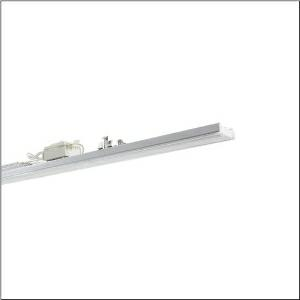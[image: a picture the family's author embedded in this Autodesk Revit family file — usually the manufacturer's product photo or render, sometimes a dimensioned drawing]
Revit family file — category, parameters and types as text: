
# Revit family: licross_21_recessed_mo_52tl11dn455g
name_source: partatom
category: Lighting Fixtures
units: mm (PartAtom-declared; Revit-internal decimal feet)

## family parameters
Cut with Voids When Loaded = No
Host = Face
Light Source = No
Part Type = Normal
Room Calculation Point = No
Round Connector Dimension = Use Diameter
Shared = No

## types (1)
- --- (1 x LED, 5800 lm, 31.8 W, 4000K)
    Apparent Load = 32 VA
    CIE Flux Codes = 89 96 99 100 100
    Color Rendering = 80
    Color Temperature = 4000K
    Default Elevation = 1800 mm
    Description = Licross 21 Recessed MO, luminaire insert, of sheet steel, galvanised, coil coated, white, length: 1.500mm, width: 66mm, height: 67mm, LED rated luminous flux: 5.800lm, light colour: 840, SDCM (Standard Deviation of Colour Matching)MacAdam ≤ 3 SDCM (initial), control gear: DALI 2, with plug, 5-pole, with phase selection, mains connection: 220..240V, AC, 50/60Hz, rated input power: 32W, internal wiring halogen-free, primary light control with lens, of plastic, primary optical cover: cover, of PMMA, light emission: direct distribution, primary light characteristic: symmetric, protection rating (complete): IP40, insulation class (complete): insulation class I (protective earthing), certification: CE, ENEC, VDE, UKCA, protection symbol: D if used in an environment without relevant dust loads with corresponding accessories, impact resistance: IK06, permissible ambient temperature for indoor applications: -25..+45°C, corresponds to IFS (International Featured Standards) requirements for safety and quality in the food industry, reducing of maximum allowable ambient temperature of 5°C with ceiling mounting, LABS conformity tested according to VDMA 24364:2018-05, The light source and the operating device comply with the requirements of the Ecodesign Regulation (EU) 2019/2020 and are replaceable in accordance with this regulation, packaging unit: 1 piece
    Height = 58 mm
    Lamp = 1 x LED
    Lamp Light Flux = 5800 lm
    Lamp Power = 31.8 W
    Lamp count = 1
    Length = 1500 mm
    Luminous efficacy = 182 lm/W
    Manufacturer = Siteco
    ModVariant = No
    Model = 52TL11DN455G
    Mounting Place = Ceiling
    Mounting Type = Pendant
    Number of Poles = 1
    OnlyDefault = Yes
    Power Factor = 1
    Product Name = Licross 21 Recessed MO
    Product group = luminaire insert | ceiling pendant
    ProductGroupID = 901
    Protection Class = Protection class I
    Protection Degree = IP 40
    RLX_Detail_Level = 1
    RLX_Emergency_Light_Flux = 0 lm
    RLX_Emergency_Type = 0
    RLX_Emergency_Type_DB = No
    RlxData = <blob elided: 24425 chars, md5=379dcfa8>
    Socket = socket
    Standby Power = 0 W
    System Light Flux = 5800 lm
    System Power = 32 W
    Type Comments = factory setting: luminous flux: 100 % | dim-lin: 254 | 215 mA
    Type Image = l_1296930.jpg
    URL = http://relux.com
    VarID = @adj_127057
    Voltage = 0 V
    Weight = 0.00 kg
    Width = 66 mm

## geometry (parser evidence)
native form markers: Blend x4, Sweep x11
no freeform markers — native parametric forms only
